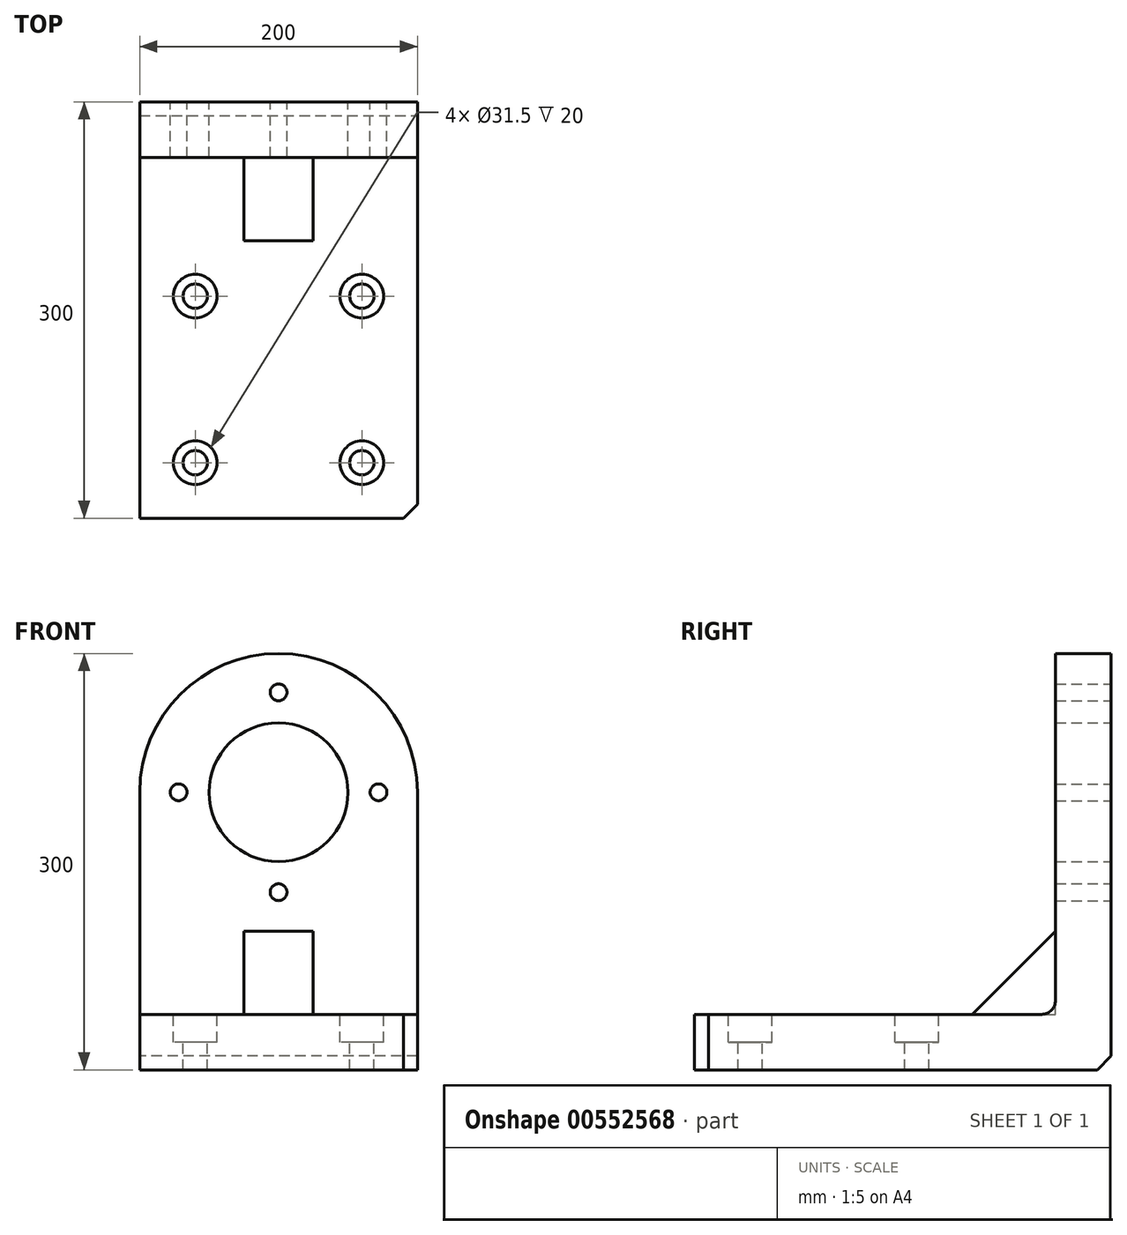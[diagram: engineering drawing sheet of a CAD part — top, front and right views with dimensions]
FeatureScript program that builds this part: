
annotation { "Feature Type Name" : "Feature", "Feature Type Description" : "" }
export const myFeature = defineFeature(function(context is Context, id is Id, definition is map)
    precondition{}
    {
        {
            var Q0;
            Q0=qCreatedBy(makeId("Front.planeOp"),FACE);
            var sketch = newSketch(context, id + "F0", { "sketchPlane" : qUnion([Q0])});
            skLineSegment(sketch, "E0", {"start": v(0, 0) * mm, "end": v(100, 0) * mm});
            skLineSegment(sketch, "E1.MirrorCS", {"start": v(0, 0) * mm, "end": v(-100, 0) * mm});
            skLineSegment(sketch, "E2", {"start": v(-100, 0) * mm, "end": v(-100, 200) * mm});
            skLineSegment(sketch, "E3", {"start": v(100, 0) * mm, "end": v(100, 200) * mm});
            skLineSegment(sketch, "E4", {"start": v(-100, 200) * mm, "end": v(100, 200) * mm, "construction": true});
            skCircle(sketch, "E5", {"center": v(0, 200) * mm, "radius": 100 * mm});
            skCircle(sketch, "E6", {"center": v(0, 200) * mm, "radius": 72 * mm, "construction": true});
            skCircle(sketch, "E7", {"center": v(0, 200) * mm, "radius": 50 * mm});
            skPoint(sketch, "E8", {"position": v(-72, 200) * mm});
            skPoint(sketch, "E9.1.0", {"position": v(0, 128) * mm});
            skPoint(sketch, "E9.2.0", {"position": v(72, 200) * mm});
            skPoint(sketch, "E9.3.0", {"position": v(0, 272) * mm});
            skLineSegment(sketch, "E10", {"start": v(-100, 0) * mm, "end": v(-100, 40) * mm});
            skLineSegment(sketch, "E11", {"start": v(-100, 40) * mm, "end": v(100, 40) * mm});
            skSolve(sketch);
        }
        {
            var Q0;
            Q0 = qSketchRegion(id + "F0", true);
            extrude(context, id + "F1", {"entities" : qUnion([Q0]), "depth" : 40 * mm, "offsetDistance" : 25 * mm});
        }
        {
            var Q0;
            Q0=sQuery(id+"F0.wireOp",VERTEX,"E9.2.0");
            var Q1;
            Q1=sQuery(id+"F0.wireOp",VERTEX,"E9.1.0");
            var Q2;
            Q2=sQuery(id+"F0.wireOp",VERTEX,"E8");
            var Q3;
            Q3=sQuery(id+"F0.wireOp",VERTEX,"E9.3.0");
            var Q4;
            Q4=makeQuery(id+"F1.opExtrude","SWEPT_BODY",BODY,{"disambiguationData":[OSD([sQuery(id+"F0.wireOp",EDGE,"E0"),sQuery(id+"F0.wireOp",EDGE,"E1.MirrorCS"),sQuery(id+"F0.wireOp",EDGE,"E2"),sQuery(id+"F0.wireOp",EDGE,"E3"),sQuery(id+"F0.wireOp",EDGE,"E5"),sQuery(id+"F0.wireOp",EDGE,"E7")])]});
            hole(context, id + "F2", {"style" : HoleStyle.SIMPLE, "endStyle" : HoleEndStyle.THROUGH, "oppositeDirection" : true, "standardTappedOrClearance" : lookupTablePath({ "standard" : "ISO", "engagement" : "75%", "pitch" : "2 mm", "size" : "M14", "type" : "Tapped" }), "standardBlindInLast" : lookupTablePath({ "standard" : "ISO", "engagement" : "75%", "pitch" : "2 mm", "size" : "M14", "type" : "Tapped" }), "holeDiameter" : 12.1 * mm, "showTappedDepth" : true, "isTappedThrough" : true, "tappedDepth" : 12 * mm, "tapClearance" : 3, "locations" : qUnion([Q0, Q1, Q2, Q3]), "scope" : qUnion([Q4]), "majorDiameter" : 14 * mm});
        }
        {
            var Q0;
            Q0=makeQuery(id+"F1.opExtrude","SWEPT_EDGE",EDGE,{"disambiguationData":[OSD([sQuery(id+"F0.wireOp",EDGE,"E1.MirrorCS"),sQuery(id+"F0.wireOp",EDGE,"E2")])]});
            var Q1;
            Q1=makeQuery(id+"F1.opExtrude","SWEPT_EDGE",EDGE,{"disambiguationData":[OSD([sQuery(id+"F0.wireOp",EDGE,"E0"),sQuery(id+"F0.wireOp",EDGE,"E3")])]});
            chamfer(context, id + "F3", {"entities" : qUnion([Q0, Q1]), "width" : 5 * mm, "tangentPropagation" : true});
        }
        {
            var Q0;
            {var subQ1=sQuery(id+"F0.wireOp",EDGE,"E0");Q0=makeQuery(id+"F0.imprint","IMPRINT",FACE,{"disambiguationData":[TD([[makeQuery(id+"F0.imprint","IMPRINT",EDGE,{"derivedFrom":subQ1}),1.0]])]});}
            extrude(context, id + "F4", {"entities" : qUnion([Q0]), "operationType" : NewBodyOperationType.ADD, "depth" : 300 * mm, "offsetDistance" : 25 * mm});
        }
        {
            var Q0;
            Q0=qCreatedBy(makeId("Right.planeOp"),FACE);
            var sketch = newSketch(context, id + "F5", { "sketchPlane" : qUnion([Q0])});
            skLineSegment(sketch, "E12.0", {"start": v(-40, 40) * mm, "end": v(-40, 200) * mm});
            skLineSegment(sketch, "E13.0", {"start": v(-300, 40) * mm, "end": v(-40, 40) * mm});
            skLineSegment(sketch, "E14", {"start": v(-100, 40) * mm, "end": v(-40, 100) * mm});
            skSolve(sketch);
        }
        {
            var Q0;
            {var subQ3=sQuery(id+"F5.wireOp",EDGE,"E14");Q0=makeQuery(id+"F5.imprint","IMPRINT",FACE,{"disambiguationData":[TD([[makeQuery(id+"F5.imprint","IMPRINT",EDGE,{"derivedFrom":subQ3}),-1.0]])]});}
            extrude(context, id + "F6", {"entities" : qUnion([Q0]), "operationType" : NewBodyOperationType.ADD, "endBound" : BoundingType.SYMMETRIC, "depth" : 50 * mm, "offsetDistance" : 25 * mm});
        }
        {
            var Q0;
            Q0=makeQuery(id+"F4.opExtrude","CAP_EDGE",EDGE,{"disambiguationData":[OSD([sQuery(id+"F0.wireOp",EDGE,"E10")])],"isStart":false});
            var Q1;
            Q1=makeQuery(id+"F4.opExtrude","CAP_EDGE",EDGE,{"disambiguationData":[OSD([sQuery(id+"F0.wireOp",EDGE,"E3")])],"isStart":false});
            var Q2;
            {var subQ0=sQuery(id+"F0.wireOp",EDGE,"E1.MirrorCS");var subQ1=sQuery(id+"F0.wireOp",EDGE,"E0");Q2=makeQuery(id+"F4.boolean.opBoolean","MERGE",EDGE,{"derivedFrom":[makeQuery(id+"F1.opExtrude","CAP_EDGE",EDGE,{"disambiguationData":[OSD([subQ1,subQ0])],"isStart":true}),makeQuery(id+"F4.opExtrude","CAP_EDGE",EDGE,{"disambiguationData":[OSD([subQ1,subQ0])],"isStart":true})]});}
            chamfer(context, id + "F7", {"entities" : qUnion([Q0, Q1, Q2]), "width" : 10 * mm, "tangentPropagation" : true});
        }
        {
            var Q0;
            {var subQ0=sQuery(id+"F0.wireOp",EDGE,"E10");var subQ1=sQuery(id+"F0.wireOp",EDGE,"E2");var subQ2=makeQuery(id+"F4.opExtrude","SWEPT_FACE",FACE,{"disambiguationData":[OSD([sQuery(id+"F0.wireOp",EDGE,"E11")])]});var subQ3=makeQuery(id+"F1.opExtrude","CAP_FACE",FACE,{"disambiguationData":[OSD([sQuery(id+"F0.wireOp",EDGE,"E0"),sQuery(id+"F0.wireOp",EDGE,"E1.MirrorCS"),subQ1,sQuery(id+"F0.wireOp",EDGE,"E3"),sQuery(id+"F0.wireOp",EDGE,"E5"),sQuery(id+"F0.wireOp",EDGE,"E7"),subQ0])],"isStart":false});Q0=makeQuery(id+"F6.boolean.opBoolean","SPLIT",EDGE,{"disambiguationData":[TD([makeQuery(id+"F4.opExtrude","SWEPT_FACE",FACE,{"disambiguationData":[OSD([subQ0])]})])],"derivedFrom":makeQuery(id+"F4.boolean.opBoolean","INTERSECT",EDGE,{"derivedFrom":[subQ3,subQ2]})});}
            var Q1;
            {var subQ0=sQuery(id+"F0.wireOp",EDGE,"E3");var subQ1=makeQuery(id+"F4.opExtrude","SWEPT_FACE",FACE,{"disambiguationData":[OSD([sQuery(id+"F0.wireOp",EDGE,"E11")])]});var subQ2=makeQuery(id+"F1.opExtrude","CAP_FACE",FACE,{"disambiguationData":[OSD([sQuery(id+"F0.wireOp",EDGE,"E0"),sQuery(id+"F0.wireOp",EDGE,"E1.MirrorCS"),sQuery(id+"F0.wireOp",EDGE,"E2"),subQ0,sQuery(id+"F0.wireOp",EDGE,"E5"),sQuery(id+"F0.wireOp",EDGE,"E7"),sQuery(id+"F0.wireOp",EDGE,"E10")])],"isStart":false});Q1=makeQuery(id+"F6.boolean.opBoolean","SPLIT",EDGE,{"disambiguationData":[TD([makeQuery(id+"F1.opExtrude","SWEPT_FACE",FACE,{"disambiguationData":[OSD([subQ0])]})])],"derivedFrom":makeQuery(id+"F4.boolean.opBoolean","INTERSECT",EDGE,{"derivedFrom":[subQ2,subQ1]})});}
            fillet(context, id + "F8", {"entities" : qUnion([Q0, Q1]), "radius" : 10 * mm, "tangentPropagation" : true, "allowEdgeOverflow" : false});
        }
        {
            var Q0;
            Q0=makeQuery(id+"F4.opExtrude","SWEPT_FACE",FACE,{"disambiguationData":[OSD([sQuery(id+"F0.wireOp",EDGE,"E11")])]});
            var sketch = newSketch(context, id + "F9", { "sketchPlane" : qUnion([Q0])});
            skPoint(sketch, "E15", {"position": v(60, -260) * mm});
            skPoint(sketch, "E16", {"position": v(-60, -260) * mm});
            skPoint(sketch, "E17", {"position": v(60, -140) * mm});
            skPoint(sketch, "E18", {"position": v(-60, -140) * mm});
            skSolve(sketch);
        }
        {
            var Q0;
            Q0=sQuery(id+"F9.wireOp",VERTEX,"E17");
            var Q1;
            Q1=sQuery(id+"F9.wireOp",VERTEX,"E15");
            var Q2;
            Q2=sQuery(id+"F9.wireOp",VERTEX,"E16");
            var Q3;
            Q3=sQuery(id+"F9.wireOp",VERTEX,"E18");
            var Q4;
            Q4=makeQuery(id+"F1.opExtrude","SWEPT_BODY",BODY,{"disambiguationData":[OSD([sQuery(id+"F0.wireOp",EDGE,"E0"),sQuery(id+"F0.wireOp",EDGE,"E1.MirrorCS"),sQuery(id+"F0.wireOp",EDGE,"E2"),sQuery(id+"F0.wireOp",EDGE,"E3"),sQuery(id+"F0.wireOp",EDGE,"E5"),sQuery(id+"F0.wireOp",EDGE,"E7"),sQuery(id+"F0.wireOp",EDGE,"E10")])]});
            hole(context, id + "F10", {"style" : HoleStyle.C_BORE, "endStyle" : HoleEndStyle.THROUGH, "holeDiameter" : 17.5 * mm, "cBoreDiameter" : 31.5 * mm, "cBoreDepth" : 20 * mm, "isTappedThrough" : true, "tappedDepth" : 12 * mm, "tapClearance" : 3, "locations" : qUnion([Q0, Q1, Q2, Q3]), "scope" : qUnion([Q4])});
        }
    });
